# Revit family: DR4030001_Ducha Monocontrol DRAA
name_source: partatom
category: Aparatos sanitarios
units: mm (PartAtom-declared; Revit-internal decimal feet)

## family parameters
Anfitrión = Muro
Compartido = No
Corte con vacíos al cargar = No
Cota de conector redondo = Diámetro de uso
Número OmniClass = 23.31.11.17.15
Punto de cálculo de habitación = No
Siempre vertical = Sí
Tipo de pieza = Normal
Título OmniClass = Shower Disc Faucets

## types (1)
- Ref. DR4030001 Ducha monocontrol
    Altura Mezclador = 1202 mm
    Altura Regadera = 2000 mm
    Ancho = 250 mm  [stored 0.82021 ft]
    Capacidad de flujo = 80 psi: 7,4 L/min.
    Creado por = IDD
    Descripción = La línea Draa cuenta con todos los atributos de diseño y funcionalidad
que la hacen perfecta para soluciones en espacios actuales. Ofrece
una línea de griferías para ducha, lavamanos y accesorios con la
perfecta combinacion de líneas rectas y modernas.
• Regadera con función de chorro tipo lluvia.
• Mayor cobertura de salida de agua.
• Tecnología que impide el taponamiento y acumulación de impurezas.
• Grifería que no contamina el agua con plomo.
• Regadera con ahorro de 7,3 litros por minuto.
    Dimensión regadera (H x L x W) = 60 x 250 x 250 mm.
2 3/8 x 9 7/8 x 9 7/8 pulg.
    Fabricante = Corona
    Fecha de creación = 29/07/2020
    Garantía = 30 años
    Garantía Acabados = 5 años
    Material = Corona_Metal
    Peso neto = 1,75 kg. - 3,85 lb.
    Presion maxima = 125 psi (862 Kpa).
    Presion minima = 20 psi (138 Kpa).
    Temperatura de uso = 5ºC a 71ºC.
    URL = https://corona.co
    Unidad monocontrol (H x L ) = 150 x 150 mm.
5 7/8 x 5 7/8 pulg.
    Vida útil = 250.000 ciclos

note: [stored X ft] marks values corroborated as IEEE doubles in the binary element streams (Revit-internal decimal feet)

## geometry (parser evidence)
native form markers: Blend x4, Extrusion x1, Sweep x14
no freeform markers — native parametric forms only
